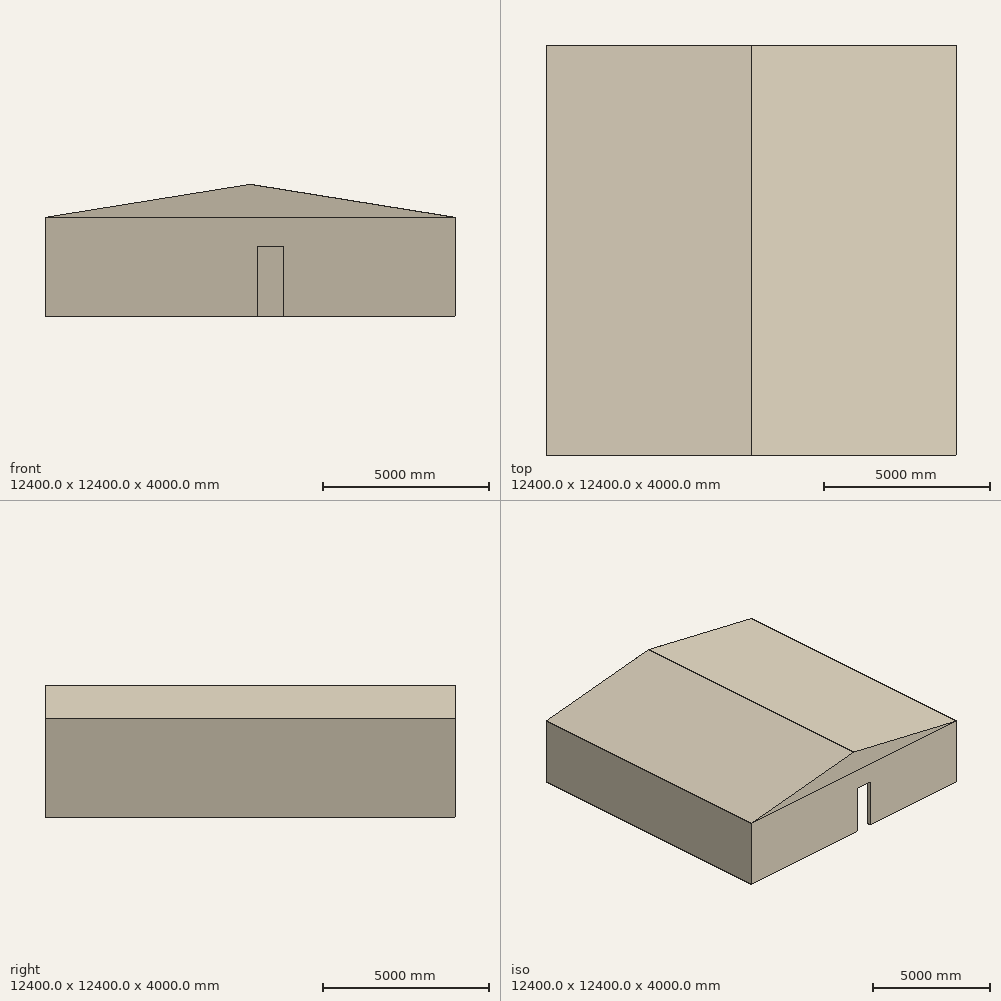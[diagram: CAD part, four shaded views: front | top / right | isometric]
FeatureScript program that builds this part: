
annotation { "Feature Type Name" : "Feature", "Feature Type Description" : "" }
export const myFeature = defineFeature(function(context is Context, id is Id, definition is map)
    precondition{}
    {
        {
            var Q0;
            Q0=qCreatedBy(makeId("Top.planeOp"),FACE);
            var sketch = newSketch(context, id + "F0", { "sketchPlane" : qUnion([Q0])});
            skLineSegment(sketch, "E0.bottom", {"start": v(6000, 6000) * mm, "end": v(5000, 6000) * mm});
            skLineSegment(sketch, "E0.top", {"start": v(6000, -6000) * mm, "end": v(1000, -6000) * mm});
            skLineSegment(sketch, "E0.left", {"start": v(6000, 6000) * mm, "end": v(6000, 2500) * mm});
            skLineSegment(sketch, "E0.right", {"start": v(-6000, 6000) * mm, "end": v(-6000, 2500) * mm});
            skPoint(sketch, "E0.middle", {"position": v(0, 0) * mm});
            skPoint(sketch, "E1", {"position": v(-6000, 0) * mm});
            skPoint(sketch, "E2", {"position": v(6000, 0) * mm});
            skPoint(sketch, "E3", {"position": v(1000, -6000) * mm});
            skPoint(sketch, "E4", {"position": v(-1000, 6000) * mm});
            skPoint(sketch, "E5", {"position": v(1000, 6000) * mm});
            skPoint(sketch, "E6", {"position": v(-1000, -6000) * mm});
            skPoint(sketch, "E7", {"position": v(-1000, 0) * mm});
            skPoint(sketch, "E8", {"position": v(1000, 0) * mm});
            skLineSegment(sketch, "E9", {"start": v(-3900, 1000) * mm, "end": v(-6000, 1000) * mm});
            skLineSegment(sketch, "E10", {"start": v(-3000, 1000) * mm, "end": v(-3000, 6000) * mm});
            skLineSegment(sketch, "E11", {"start": v(-5000, 6000) * mm, "end": v(-5000, 3100) * mm});
            skLineSegment(sketch, "E12", {"start": v(-4900, 2500) * mm, "end": v(-6000, 2500) * mm});
            skLineSegment(sketch, "E13.0", {"start": v(-4900, 6000) * mm, "end": v(-4900, 3100) * mm});
            skLineSegment(sketch, "E14.0", {"start": v(-4900, 2400) * mm, "end": v(-6000, 2400) * mm});
            skLineSegment(sketch, "E15.0", {"start": v(-3900, 1100) * mm, "end": v(-6000, 1100) * mm});
            skLineSegment(sketch, "E16.0", {"start": v(-3100, 1000) * mm, "end": v(-3100, 6000) * mm});
            skLineSegment(sketch, "E17", {"start": v(-4900, 2400) * mm, "end": v(-4900, 2500) * mm});
            skLineSegment(sketch, "E18", {"start": v(-4900, 3100) * mm, "end": v(-5000, 3100) * mm});
            skLineSegment(sketch, "E19", {"start": v(-3900, 1000) * mm, "end": v(-3900, 1100) * mm});
            skLineSegment(sketch, "E20", {"start": v(-3100, 1000) * mm, "end": v(-3000, 1000) * mm});
            skLineSegment(sketch, "E21.0", {"start": v(-6200, 6200) * mm, "end": v(-6200, -6200) * mm});
            skLineSegment(sketch, "E21.1", {"start": v(6200, 6200) * mm, "end": v(-6200, 6200) * mm});
            skLineSegment(sketch, "E21.2", {"start": v(6200, 6200) * mm, "end": v(6200, -6200) * mm});
            skLineSegment(sketch, "E21.3", {"start": v(6200, -6200) * mm, "end": v(1000, -6200) * mm});
            skLineSegment(sketch, "E22.MirrorCS", {"start": v(-1100, 3100) * mm, "end": v(-1000, 3100) * mm});
            skLineSegment(sketch, "E23.MirrorCS", {"start": v(-1100, 2400) * mm, "end": v(-1100, 2500) * mm});
            skLineSegment(sketch, "E24.MirrorCS", {"start": v(-1100, 2400) * mm, "end": v(-50, 2400) * mm});
            skLineSegment(sketch, "E25.MirrorCS", {"start": v(-2100, 1100) * mm, "end": v(-50, 1100) * mm});
            skLineSegment(sketch, "E26.MirrorCS", {"start": v(-2100, 1000) * mm, "end": v(0, 1000) * mm});
            skLineSegment(sketch, "E27.MirrorCS", {"start": v(-1000, 6000) * mm, "end": v(-1000, 3100) * mm});
            skLineSegment(sketch, "E28.MirrorCS", {"start": v(-1100, 2500) * mm, "end": v(-50, 2500) * mm});
            skLineSegment(sketch, "E29.MirrorCS", {"start": v(-1100, 6000) * mm, "end": v(-1100, 3100) * mm});
            skLineSegment(sketch, "E30", {"start": v(0, 6000) * mm, "end": v(0, -6000) * mm, "construction": true});
            skLineSegment(sketch, "E31.MirrorCS", {"start": v(1100, 2400) * mm, "end": v(1100, 2500) * mm});
            skLineSegment(sketch, "E32.MirrorCS", {"start": v(1100, 3100) * mm, "end": v(1000, 3100) * mm});
            skLineSegment(sketch, "E33.MirrorCS", {"start": v(4900, 2400) * mm, "end": v(4900, 2500) * mm});
            skLineSegment(sketch, "E34.MirrorCS", {"start": v(3100, 1000) * mm, "end": v(3000, 1000) * mm});
            skLineSegment(sketch, "E35.MirrorCS", {"start": v(3900, 1000) * mm, "end": v(3900, 1100) * mm});
            skLineSegment(sketch, "E36.MirrorCS", {"start": v(4900, 3100) * mm, "end": v(5000, 3100) * mm});
            skLineSegment(sketch, "E37.MirrorCS", {"start": v(4900, 2400) * mm, "end": v(6000, 2400) * mm});
            skLineSegment(sketch, "E38.MirrorCS", {"start": v(2100, 1000) * mm, "end": v(0, 1000) * mm});
            skLineSegment(sketch, "E39.MirrorCS", {"start": v(2100, 1100) * mm, "end": v(50, 1100) * mm});
            skLineSegment(sketch, "E40.MirrorCS", {"start": v(1100, 6000) * mm, "end": v(1100, 3100) * mm});
            skLineSegment(sketch, "E41.MirrorCS", {"start": v(1100, 2400) * mm, "end": v(50, 2400) * mm});
            skLineSegment(sketch, "E42.MirrorCS", {"start": v(1100, 2500) * mm, "end": v(50, 2500) * mm});
            skLineSegment(sketch, "E43.MirrorCS", {"start": v(3100, 1000) * mm, "end": v(3100, 6000) * mm});
            skLineSegment(sketch, "E44.MirrorCS", {"start": v(3900, 1100) * mm, "end": v(6000, 1100) * mm});
            skLineSegment(sketch, "E45.MirrorCS", {"start": v(4900, 6000) * mm, "end": v(4900, 3100) * mm});
            skLineSegment(sketch, "E46.MirrorCS", {"start": v(4900, 2500) * mm, "end": v(6000, 2500) * mm});
            skLineSegment(sketch, "E47.MirrorCS", {"start": v(5000, 6000) * mm, "end": v(5000, 3100) * mm});
            skLineSegment(sketch, "E48.MirrorCS", {"start": v(3000, 1000) * mm, "end": v(3000, 6000) * mm});
            skLineSegment(sketch, "E49.MirrorCS", {"start": v(1000, 6000) * mm, "end": v(1000, 3100) * mm});
            skLineSegment(sketch, "E50.MirrorCS", {"start": v(3900, 1000) * mm, "end": v(6000, 1000) * mm});
            skLineSegment(sketch, "E51.left", {"start": v(50, 6000) * mm, "end": v(50, 2500) * mm});
            skLineSegment(sketch, "E51.right", {"start": v(-50, 6000) * mm, "end": v(-50, 2500) * mm});
            skPoint(sketch, "E51.middle", {"position": v(0, 4250) * mm});
            skLineSegment(sketch, "E52", {"start": v(-6000, 0) * mm, "end": v(-1900, 0) * mm});
            skLineSegment(sketch, "E53", {"start": v(-1000, 0) * mm, "end": v(-1000, -3200) * mm});
            skLineSegment(sketch, "E54", {"start": v(-4500, -6000) * mm, "end": v(-4500, -5400) * mm});
            skLineSegment(sketch, "E55", {"start": v(-4500, -5400) * mm, "end": v(-1000, -5400) * mm});
            skLineSegment(sketch, "E56", {"start": v(-1000, -5400) * mm, "end": v(-1000, -4000) * mm});
            skLineSegment(sketch, "E57", {"start": v(-6000, -2100) * mm, "end": v(-3100, -2100) * mm});
            skLineSegment(sketch, "E58", {"start": v(6000, 0) * mm, "end": v(1000, 0) * mm});
            skLineSegment(sketch, "E59", {"start": v(6000, -2200) * mm, "end": v(1000, -2200) * mm});
            skLineSegment(sketch, "E60", {"start": v(1000, 0) * mm, "end": v(1000, -1300) * mm});
            skLineSegment(sketch, "E61.0", {"start": v(-6000, -100) * mm, "end": v(-1900, -100) * mm});
            skLineSegment(sketch, "E62.0", {"start": v(-2500, -3100) * mm, "end": v(-2500, -2000) * mm});
            skLineSegment(sketch, "E63.0", {"start": v(-6000, -2000) * mm, "end": v(-3100, -2000) * mm});
            skLineSegment(sketch, "E64.0", {"start": v(-1100, 0) * mm, "end": v(-1100, -3100) * mm});
            skLineSegment(sketch, "E65.0", {"start": v(-1100, -5300) * mm, "end": v(-1100, -4000) * mm});
            skLineSegment(sketch, "E65.1", {"start": v(-4600, -5300) * mm, "end": v(-1100, -5300) * mm});
            skLineSegment(sketch, "E65.2", {"start": v(-4600, -6000) * mm, "end": v(-4600, -5300) * mm});
            skLineSegment(sketch, "E66.0", {"start": v(1100, -100) * mm, "end": v(1100, -1300) * mm});
            skLineSegment(sketch, "E66.1", {"start": v(6000, -100) * mm, "end": v(1100, -100) * mm});
            skLineSegment(sketch, "E67.0", {"start": v(6000, -2100) * mm, "end": v(1000, -2100) * mm});
            skLineSegment(sketch, "E68.0", {"start": v(-2400, -3100) * mm, "end": v(-2400, -2000) * mm});
            skLineSegment(sketch, "E69", {"start": v(-3100, -2000) * mm, "end": v(-3100, -2100) * mm});
            skLineSegment(sketch, "E70", {"start": v(-2500, -2000) * mm, "end": v(-2400, -2000) * mm});
            skLineSegment(sketch, "E71", {"start": v(-1100, 0) * mm, "end": v(-1000, 0) * mm});
            skLineSegment(sketch, "E72", {"start": v(-1100, -4000) * mm, "end": v(-1000, -4000) * mm});
            skLineSegment(sketch, "E73", {"start": v(-1900, -100) * mm, "end": v(-1900, 0) * mm});
            skLineSegment(sketch, "E74", {"start": v(1000, -1300) * mm, "end": v(1100, -1300) * mm});
            skLineSegment(sketch, "E75", {"start": v(1000, -2100) * mm, "end": v(1000, -2200) * mm});
            skLineSegment(sketch, "E76", {"start": v(1000, -6000) * mm, "end": v(1000, -6200) * mm});
            skLineSegment(sketch, "E77", {"start": v(200, -6000) * mm, "end": v(200, -6200) * mm});
            skLineSegment(sketch, "E78", {"start": v(-1100, -3100) * mm, "end": v(-2400, -3100) * mm});
            skLineSegment(sketch, "E79.0", {"start": v(-1000, -3200) * mm, "end": v(-6000, -3200) * mm});
            skLineSegment(sketch, "E80.trimOffspring", {"start": v(-6000, -3200) * mm, "end": v(-6000, -6000) * mm});
            skLineSegment(sketch, "E81.trimOffspring", {"start": v(-2500, -3100) * mm, "end": v(-6000, -3100) * mm});
            skLineSegment(sketch, "E82.trimOffspring", {"start": v(-4600, -6000) * mm, "end": v(-6000, -6000) * mm});
            skLineSegment(sketch, "E83.trimOffspring", {"start": v(-6000, -2100) * mm, "end": v(-6000, -3100) * mm});
            skLineSegment(sketch, "E84.trimOffspring", {"start": v(-6000, 1000) * mm, "end": v(-6000, 0) * mm});
            skLineSegment(sketch, "E85.trimOffspring", {"start": v(-6000, -100) * mm, "end": v(-6000, -2000) * mm});
            skLineSegment(sketch, "E86.trimOffspring", {"start": v(-6000, 2400) * mm, "end": v(-6000, 1100) * mm});
            skLineSegment(sketch, "E87.trimOffspring", {"start": v(-5000, 6000) * mm, "end": v(-6000, 6000) * mm});
            skLineSegment(sketch, "E88.trimOffspring", {"start": v(-1100, 6000) * mm, "end": v(-3000, 6000) * mm});
            skLineSegment(sketch, "E89.trimOffspring", {"start": v(-3100, 6000) * mm, "end": v(-4900, 6000) * mm});
            skLineSegment(sketch, "E90.trimOffspring", {"start": v(-50, 6000) * mm, "end": v(-1000, 6000) * mm});
            skLineSegment(sketch, "E91.trimOffspring", {"start": v(1000, 6000) * mm, "end": v(50, 6000) * mm});
            skLineSegment(sketch, "E92.trimOffspring", {"start": v(3000, 6000) * mm, "end": v(1100, 6000) * mm});
            skLineSegment(sketch, "E93.trimOffspring", {"start": v(4900, 6000) * mm, "end": v(3100, 6000) * mm});
            skLineSegment(sketch, "E94.trimOffspring", {"start": v(6000, -100) * mm, "end": v(6000, -2100) * mm});
            skLineSegment(sketch, "E95.trimOffspring", {"start": v(6000, -2200) * mm, "end": v(6000, -6000) * mm});
            skLineSegment(sketch, "E96.trimOffspring", {"start": v(6000, 2400) * mm, "end": v(6000, 1100) * mm});
            skLineSegment(sketch, "E97.trimOffspring", {"start": v(6000, 1000) * mm, "end": v(6000, 0) * mm});
            skLineSegment(sketch, "E98.trimOffspring", {"start": v(200, -6000) * mm, "end": v(-4500, -6000) * mm});
            skLineSegment(sketch, "E99.trimOffspring", {"start": v(200, -6200) * mm, "end": v(-6200, -6200) * mm});
            skPoint(sketch, "E100.orphan", {"position": v(0, 2500) * mm});
            skLineSegment(sketch, "E101", {"start": v(-50, 2400) * mm, "end": v(-50, 1100) * mm});
            skLineSegment(sketch, "E102", {"start": v(50, 2400) * mm, "end": v(50, 1100) * mm});
            skPoint(sketch, "E103.orphan", {"position": v(0, 2400) * mm});
            skPoint(sketch, "E104.orphan", {"position": v(0, 1100) * mm});
            skLineSegment(sketch, "E105", {"start": v(-2100, 1100) * mm, "end": v(-2200, 1100) * mm});
            skLineSegment(sketch, "E106", {"start": v(-2200, 1100) * mm, "end": v(-2200, 1000) * mm});
            skLineSegment(sketch, "E107", {"start": v(-2200, 1000) * mm, "end": v(-2100, 1000) * mm});
            skLineSegment(sketch, "E108.MirrorCS", {"start": v(2200, 1000) * mm, "end": v(2100, 1000) * mm});
            skLineSegment(sketch, "E109.MirrorCS", {"start": v(2100, 1100) * mm, "end": v(2200, 1100) * mm});
            skLineSegment(sketch, "E110.MirrorCS", {"start": v(2200, 1100) * mm, "end": v(2200, 1000) * mm});
            skSolve(sketch);
        }
        {
            var Q0;
            Q0 = qSketchRegion(id + "F0", true);
            extrude(context, id + "F1", {"entities" : qUnion([Q0]), "depth" : 2120 * mm});
        }
        {
            var Q0;
            Q0=makeQuery(id+"F1.opExtrude","CAP_FACE",FACE,{"disambiguationData":[OSD([sQuery(id+"F0.wireOp",EDGE,"E0.bottom"),sQuery(id+"F0.wireOp",EDGE,"E0.top"),sQuery(id+"F0.wireOp",EDGE,"E0.left"),sQuery(id+"F0.wireOp",EDGE,"E0.right"),sQuery(id+"F0.wireOp",EDGE,"E9"),sQuery(id+"F0.wireOp",EDGE,"E10"),sQuery(id+"F0.wireOp",EDGE,"E11"),sQuery(id+"F0.wireOp",EDGE,"E12"),sQuery(id+"F0.wireOp",EDGE,"E13.0"),sQuery(id+"F0.wireOp",EDGE,"E14.0"),sQuery(id+"F0.wireOp",EDGE,"E15.0"),sQuery(id+"F0.wireOp",EDGE,"E16.0"),sQuery(id+"F0.wireOp",EDGE,"E17"),sQuery(id+"F0.wireOp",EDGE,"E18"),sQuery(id+"F0.wireOp",EDGE,"E19"),sQuery(id+"F0.wireOp",EDGE,"E20"),sQuery(id+"F0.wireOp",EDGE,"E21.0"),sQuery(id+"F0.wireOp",EDGE,"E21.1"),sQuery(id+"F0.wireOp",EDGE,"E21.2"),sQuery(id+"F0.wireOp",EDGE,"E21.3"),sQuery(id+"F0.wireOp",EDGE,"E22.MirrorCS"),sQuery(id+"F0.wireOp",EDGE,"E23.MirrorCS"),sQuery(id+"F0.wireOp",EDGE,"E24.MirrorCS"),sQuery(id+"F0.wireOp",EDGE,"E25.MirrorCS"),sQuery(id+"F0.wireOp",EDGE,"E26.MirrorCS"),sQuery(id+"F0.wireOp",EDGE,"E27.MirrorCS"),sQuery(id+"F0.wireOp",EDGE,"E28.MirrorCS"),sQuery(id+"F0.wireOp",EDGE,"E29.MirrorCS"),sQuery(id+"F0.wireOp",EDGE,"E31.MirrorCS"),sQuery(id+"F0.wireOp",EDGE,"E32.MirrorCS"),sQuery(id+"F0.wireOp",EDGE,"E33.MirrorCS"),sQuery(id+"F0.wireOp",EDGE,"E34.MirrorCS"),sQuery(id+"F0.wireOp",EDGE,"E35.MirrorCS"),sQuery(id+"F0.wireOp",EDGE,"E36.MirrorCS"),sQuery(id+"F0.wireOp",EDGE,"E37.MirrorCS"),sQuery(id+"F0.wireOp",EDGE,"E38.MirrorCS"),sQuery(id+"F0.wireOp",EDGE,"E39.MirrorCS"),sQuery(id+"F0.wireOp",EDGE,"E40.MirrorCS"),sQuery(id+"F0.wireOp",EDGE,"E41.MirrorCS"),sQuery(id+"F0.wireOp",EDGE,"E42.MirrorCS"),sQuery(id+"F0.wireOp",EDGE,"E43.MirrorCS"),sQuery(id+"F0.wireOp",EDGE,"E44.MirrorCS"),sQuery(id+"F0.wireOp",EDGE,"E45.MirrorCS"),sQuery(id+"F0.wireOp",EDGE,"E46.MirrorCS"),sQuery(id+"F0.wireOp",EDGE,"E47.MirrorCS"),sQuery(id+"F0.wireOp",EDGE,"E48.MirrorCS"),sQuery(id+"F0.wireOp",EDGE,"E49.MirrorCS"),sQuery(id+"F0.wireOp",EDGE,"E50.MirrorCS"),sQuery(id+"F0.wireOp",EDGE,"E51.left"),sQuery(id+"F0.wireOp",EDGE,"E51.right"),sQuery(id+"F0.wireOp",EDGE,"E52"),sQuery(id+"F0.wireOp",EDGE,"E53"),sQuery(id+"F0.wireOp",EDGE,"E54"),sQuery(id+"F0.wireOp",EDGE,"E55"),sQuery(id+"F0.wireOp",EDGE,"E56"),sQuery(id+"F0.wireOp",EDGE,"E57"),sQuery(id+"F0.wireOp",EDGE,"E58"),sQuery(id+"F0.wireOp",EDGE,"E59"),sQuery(id+"F0.wireOp",EDGE,"E60"),sQuery(id+"F0.wireOp",EDGE,"E61.0"),sQuery(id+"F0.wireOp",EDGE,"E62.0"),sQuery(id+"F0.wireOp",EDGE,"E63.0"),sQuery(id+"F0.wireOp",EDGE,"E64.0"),sQuery(id+"F0.wireOp",EDGE,"E65.0"),sQuery(id+"F0.wireOp",EDGE,"E65.1"),sQuery(id+"F0.wireOp",EDGE,"E65.2"),sQuery(id+"F0.wireOp",EDGE,"E66.0"),sQuery(id+"F0.wireOp",EDGE,"E66.1"),sQuery(id+"F0.wireOp",EDGE,"E67.0"),sQuery(id+"F0.wireOp",EDGE,"E68.0"),sQuery(id+"F0.wireOp",EDGE,"E69"),sQuery(id+"F0.wireOp",EDGE,"E70"),sQuery(id+"F0.wireOp",EDGE,"E71"),sQuery(id+"F0.wireOp",EDGE,"E72"),sQuery(id+"F0.wireOp",EDGE,"E73"),sQuery(id+"F0.wireOp",EDGE,"E74"),sQuery(id+"F0.wireOp",EDGE,"E75"),sQuery(id+"F0.wireOp",EDGE,"E76"),sQuery(id+"F0.wireOp",EDGE,"E77"),sQuery(id+"F0.wireOp",EDGE,"E78"),sQuery(id+"F0.wireOp",EDGE,"E79.0"),sQuery(id+"F0.wireOp",EDGE,"E80.trimOffspring"),sQuery(id+"F0.wireOp",EDGE,"E81.trimOffspring"),sQuery(id+"F0.wireOp",EDGE,"E82.trimOffspring"),sQuery(id+"F0.wireOp",EDGE,"E83.trimOffspring"),sQuery(id+"F0.wireOp",EDGE,"E84.trimOffspring"),sQuery(id+"F0.wireOp",EDGE,"E85.trimOffspring"),sQuery(id+"F0.wireOp",EDGE,"E86.trimOffspring"),sQuery(id+"F0.wireOp",EDGE,"E87.trimOffspring"),sQuery(id+"F0.wireOp",EDGE,"E88.trimOffspring"),sQuery(id+"F0.wireOp",EDGE,"E89.trimOffspring"),sQuery(id+"F0.wireOp",EDGE,"E90.trimOffspring"),sQuery(id+"F0.wireOp",EDGE,"E91.trimOffspring"),sQuery(id+"F0.wireOp",EDGE,"E92.trimOffspring"),sQuery(id+"F0.wireOp",EDGE,"E93.trimOffspring"),sQuery(id+"F0.wireOp",EDGE,"E94.trimOffspring"),sQuery(id+"F0.wireOp",EDGE,"E95.trimOffspring"),sQuery(id+"F0.wireOp",EDGE,"E96.trimOffspring"),sQuery(id+"F0.wireOp",EDGE,"E97.trimOffspring"),sQuery(id+"F0.wireOp",EDGE,"E98.trimOffspring"),sQuery(id+"F0.wireOp",EDGE,"E99.trimOffspring"),sQuery(id+"F0.wireOp",EDGE,"E101"),sQuery(id+"F0.wireOp",EDGE,"E102"),sQuery(id+"F0.wireOp",EDGE,"E105"),sQuery(id+"F0.wireOp",EDGE,"E106"),sQuery(id+"F0.wireOp",EDGE,"E107"),sQuery(id+"F0.wireOp",EDGE,"E108.MirrorCS"),sQuery(id+"F0.wireOp",EDGE,"E109.MirrorCS"),sQuery(id+"F0.wireOp",EDGE,"E110.MirrorCS")])],"isStart":false});
            var sketch = newSketch(context, id + "F2", { "sketchPlane" : qUnion([Q0])});
            skLineSegment(sketch, "E111.0", {"start": v(-6200, 6200) * mm, "end": v(-6200, -6200) * mm});
            skLineSegment(sketch, "E112.0", {"start": v(6200, 6200) * mm, "end": v(-6200, 6200) * mm});
            skLineSegment(sketch, "E113.0", {"start": v(6200, 6200) * mm, "end": v(6200, -6200) * mm});
            skLineSegment(sketch, "E114.0", {"start": v(-5000, 6000) * mm, "end": v(-6000, 6000) * mm});
            skLineSegment(sketch, "E115.0", {"start": v(-6000, 6000) * mm, "end": v(-6000, 2500) * mm});
            skLineSegment(sketch, "E116.0", {"start": v(-4900, 2400) * mm, "end": v(-6000, 2400) * mm});
            skLineSegment(sketch, "E117.0", {"start": v(-6000, 2400) * mm, "end": v(-6000, 1100) * mm});
            skLineSegment(sketch, "E118.0", {"start": v(-6000, 1000) * mm, "end": v(-6000, 0) * mm});
            skLineSegment(sketch, "E119.0", {"start": v(-3100, 6000) * mm, "end": v(-4900, 6000) * mm});
            skLineSegment(sketch, "E120.0", {"start": v(-1100, 6000) * mm, "end": v(-3000, 6000) * mm});
            skLineSegment(sketch, "E121.0", {"start": v(-50, 6000) * mm, "end": v(-1000, 6000) * mm});
            skLineSegment(sketch, "E122.0", {"start": v(1000, 6000) * mm, "end": v(50, 6000) * mm});
            skLineSegment(sketch, "E123.0", {"start": v(3000, 6000) * mm, "end": v(1100, 6000) * mm});
            skLineSegment(sketch, "E124.0", {"start": v(4900, 6000) * mm, "end": v(3100, 6000) * mm});
            skLineSegment(sketch, "E125.0", {"start": v(6000, 6000) * mm, "end": v(5000, 6000) * mm});
            skLineSegment(sketch, "E126.0", {"start": v(6000, 6000) * mm, "end": v(6000, 2500) * mm});
            skLineSegment(sketch, "E127.0", {"start": v(4900, 2400) * mm, "end": v(6000, 2400) * mm});
            skLineSegment(sketch, "E128.0", {"start": v(1100, 2400) * mm, "end": v(50, 2400) * mm});
            skLineSegment(sketch, "E129.0", {"start": v(50, 2400) * mm, "end": v(50, 1100) * mm});
            skLineSegment(sketch, "E130.0", {"start": v(-50, 2400) * mm, "end": v(-50, 1100) * mm});
            skLineSegment(sketch, "E131.0", {"start": v(-1100, 2400) * mm, "end": v(-50, 2400) * mm});
            skLineSegment(sketch, "E132.0", {"start": v(6000, 1000) * mm, "end": v(6000, 0) * mm});
            skLineSegment(sketch, "E133.0", {"start": v(6000, -2200) * mm, "end": v(1000, -2200) * mm});
            skLineSegment(sketch, "E134.0", {"start": v(6000, -100) * mm, "end": v(6000, -2100) * mm});
            skLineSegment(sketch, "E135.0", {"start": v(6000, 0) * mm, "end": v(1000, 0) * mm});
            skLineSegment(sketch, "E136.0", {"start": v(6000, -100) * mm, "end": v(1100, -100) * mm});
            skLineSegment(sketch, "E137.0", {"start": v(-2400, -3100) * mm, "end": v(-2400, -2000) * mm});
            skLineSegment(sketch, "E138.0", {"start": v(-1100, -3100) * mm, "end": v(-2400, -3100) * mm});
            skLineSegment(sketch, "E139.0", {"start": v(-2500, -3100) * mm, "end": v(-6000, -3100) * mm});
            skLineSegment(sketch, "E140.0", {"start": v(-6000, -2100) * mm, "end": v(-6000, -3100) * mm});
            skLineSegment(sketch, "E141.0", {"start": v(-6000, -100) * mm, "end": v(-6000, -2000) * mm});
            skLineSegment(sketch, "E142.0", {"start": v(-6000, -3200) * mm, "end": v(-6000, -6000) * mm});
            skLineSegment(sketch, "E143.0", {"start": v(-4600, -6000) * mm, "end": v(-6000, -6000) * mm});
            skLineSegment(sketch, "E144.0", {"start": v(-4600, -6000) * mm, "end": v(-4600, -5300) * mm});
            skLineSegment(sketch, "E145.0", {"start": v(-4600, -5300) * mm, "end": v(-1100, -5300) * mm});
            skLineSegment(sketch, "E146.0", {"start": v(-4500, -6000) * mm, "end": v(-4500, -5400) * mm});
            skLineSegment(sketch, "E147.0", {"start": v(6000, -2200) * mm, "end": v(6000, -6000) * mm});
            skLineSegment(sketch, "E148", {"start": v(-4900, 2400) * mm, "end": v(-4900, 6000) * mm});
            skLineSegment(sketch, "E149", {"start": v(-5000, 6000) * mm, "end": v(-5000, 2500) * mm});
            skLineSegment(sketch, "E150", {"start": v(-6000, 2500) * mm, "end": v(-5000, 2500) * mm});
            skLineSegment(sketch, "E151", {"start": v(-6000, 1100) * mm, "end": v(-3100, 1100) * mm});
            skLineSegment(sketch, "E152", {"start": v(-3100, 1100) * mm, "end": v(-3100, 6000) * mm});
            skLineSegment(sketch, "E153.0", {"start": v(-50, 6000) * mm, "end": v(-50, 2500) * mm});
            skLineSegment(sketch, "E154.0", {"start": v(50, 6000) * mm, "end": v(50, 2500) * mm});
            skLineSegment(sketch, "E155", {"start": v(-1000, 6000) * mm, "end": v(-1000, 2500) * mm});
            skLineSegment(sketch, "E156", {"start": v(-1000, 2500) * mm, "end": v(-50, 2500) * mm});
            skLineSegment(sketch, "E157", {"start": v(-1100, 2400) * mm, "end": v(-1100, 6000) * mm});
            skLineSegment(sketch, "E158", {"start": v(1000, 6000) * mm, "end": v(1000, 2500) * mm});
            skLineSegment(sketch, "E159", {"start": v(50, 2500) * mm, "end": v(1000, 2500) * mm});
            skLineSegment(sketch, "E160", {"start": v(1100, 2400) * mm, "end": v(1100, 6000) * mm});
            skLineSegment(sketch, "E161", {"start": v(5000, 6000) * mm, "end": v(5000, 2500) * mm});
            skLineSegment(sketch, "E162", {"start": v(6000, 2500) * mm, "end": v(5000, 2500) * mm});
            skLineSegment(sketch, "E163", {"start": v(4900, 2400) * mm, "end": v(4900, 6000) * mm});
            skLineSegment(sketch, "E164.0", {"start": v(6000, 2400) * mm, "end": v(6000, 1100) * mm});
            skLineSegment(sketch, "E165", {"start": v(3100, 6000) * mm, "end": v(3100, 1100) * mm});
            skLineSegment(sketch, "E166", {"start": v(6000, 1100) * mm, "end": v(3100, 1100) * mm});
            skLineSegment(sketch, "E167", {"start": v(-3000, 6000) * mm, "end": v(-3000, 1100) * mm});
            skLineSegment(sketch, "E168", {"start": v(3000, 6000) * mm, "end": v(3000, 1100) * mm});
            skLineSegment(sketch, "E169", {"start": v(50, 1100) * mm, "end": v(3000, 1100) * mm});
            skLineSegment(sketch, "E170", {"start": v(-50, 1100) * mm, "end": v(-3000, 1100) * mm});
            skLineSegment(sketch, "E171", {"start": v(-6000, 1000) * mm, "end": v(6000, 1000) * mm});
            skLineSegment(sketch, "E172", {"start": v(-6000, -2100) * mm, "end": v(-2500, -2100) * mm});
            skLineSegment(sketch, "E173", {"start": v(-2500, -2100) * mm, "end": v(-2500, -3100) * mm});
            skLineSegment(sketch, "E174", {"start": v(-2400, -2000) * mm, "end": v(-6000, -2000) * mm});
            skLineSegment(sketch, "E175", {"start": v(-6000, -100) * mm, "end": v(-1100, -100) * mm});
            skLineSegment(sketch, "E176", {"start": v(-1100, -3100) * mm, "end": v(-1100, -100) * mm});
            skLineSegment(sketch, "E177", {"start": v(-1000, 0) * mm, "end": v(-6000, 0) * mm});
            skLineSegment(sketch, "E178", {"start": v(1100, -100) * mm, "end": v(1100, -2100) * mm});
            skLineSegment(sketch, "E179", {"start": v(1100, -2100) * mm, "end": v(6000, -2100) * mm});
            skLineSegment(sketch, "E180", {"start": v(1000, -2200) * mm, "end": v(1000, 0) * mm});
            skLineSegment(sketch, "E181", {"start": v(-1100, -3200) * mm, "end": v(-6000, -3200) * mm});
            skLineSegment(sketch, "E182", {"start": v(-1100, -3200) * mm, "end": v(-1100, -5300) * mm});
            skLineSegment(sketch, "E183", {"start": v(-4500, -5400) * mm, "end": v(-1100, -5400) * mm});
            skLineSegment(sketch, "E184", {"start": v(-1100, -6000) * mm, "end": v(-1100, -5400) * mm});
            skLineSegment(sketch, "E185", {"start": v(-1100, -6000) * mm, "end": v(-4500, -6000) * mm});
            skLineSegment(sketch, "E186", {"start": v(-1000, 0) * mm, "end": v(-1000, -6000) * mm});
            skLineSegment(sketch, "E187", {"start": v(-1000, -6000) * mm, "end": v(6000, -6000) * mm});
            skLineSegment(sketch, "E188", {"start": v(-6200, -6200) * mm, "end": v(6200, -6200) * mm});
            skSolve(sketch);
        }
        {
            var Q0;
            {var subQ10=sQuery(id+"F2.wireOp",EDGE,"E111.0");Q0=makeQuery(id+"F2.imprint","IMPRINT",FACE,{"disambiguationData":[TD([[makeQuery(id+"F2.imprint","IMPRINT",EDGE,{"derivedFrom":subQ10}),1.0]])]});}
            var Q1;
            {var subQ1=makeQuery(id+"F1.opExtrude","CAP_EDGE",EDGE,{"disambiguationData":[OSD([sQuery(id+"F0.wireOp",EDGE,"E76")])],"isStart":false});Q1=makeQuery(id+"F2.imprint","IMPRINT",FACE,{"disambiguationData":[TD([[makeQuery(id+"F2.imprint","IMPRINT",EDGE,{"derivedFrom":subQ1}),-1.0]])]});}
            var Q2;
            {var subQ1=makeQuery(id+"F1.opExtrude","CAP_EDGE",EDGE,{"disambiguationData":[OSD([sQuery(id+"F0.wireOp",EDGE,"E72")])],"isStart":false});Q2=makeQuery(id+"F2.imprint","IMPRINT",FACE,{"disambiguationData":[TD([[makeQuery(id+"F2.imprint","IMPRINT",EDGE,{"derivedFrom":subQ1}),1.0]])]});}
            var Q3;
            {var subQ0=sQuery(id+"F2.wireOp",EDGE,"E184");Q3=makeQuery(id+"F2.imprint","IMPRINT",FACE,{"disambiguationData":[TD([[makeQuery(id+"F2.imprint","IMPRINT",EDGE,{"derivedFrom":subQ0}),-1.0]])]});}
            var Q4;
            {var subQ1=makeQuery(id+"F1.opExtrude","CAP_EDGE",EDGE,{"disambiguationData":[OSD([sQuery(id+"F0.wireOp",EDGE,"E69")])],"isStart":false});Q4=makeQuery(id+"F2.imprint","IMPRINT",FACE,{"disambiguationData":[TD([[makeQuery(id+"F2.imprint","IMPRINT",EDGE,{"derivedFrom":subQ1}),1.0]])]});}
            var Q5;
            {var subQ1=makeQuery(id+"F1.opExtrude","CAP_EDGE",EDGE,{"disambiguationData":[OSD([sQuery(id+"F0.wireOp",EDGE,"E73")])],"isStart":false});Q5=makeQuery(id+"F2.imprint","IMPRINT",FACE,{"disambiguationData":[TD([[makeQuery(id+"F2.imprint","IMPRINT",EDGE,{"derivedFrom":subQ1}),-1.0]])]});}
            var Q6;
            {var subQ1=makeQuery(id+"F1.opExtrude","CAP_EDGE",EDGE,{"disambiguationData":[OSD([sQuery(id+"F0.wireOp",EDGE,"E74")])],"isStart":false});Q6=makeQuery(id+"F2.imprint","IMPRINT",FACE,{"disambiguationData":[TD([[makeQuery(id+"F2.imprint","IMPRINT",EDGE,{"derivedFrom":subQ1}),-1.0]])]});}
            var Q7;
            {var subQ1=makeQuery(id+"F1.opExtrude","CAP_EDGE",EDGE,{"disambiguationData":[OSD([sQuery(id+"F0.wireOp",EDGE,"E106")])],"isStart":false});Q7=makeQuery(id+"F2.imprint","IMPRINT",FACE,{"disambiguationData":[TD([[makeQuery(id+"F2.imprint","IMPRINT",EDGE,{"derivedFrom":subQ1}),-1.0]])]});}
            var Q8;
            {var subQ1=makeQuery(id+"F1.opExtrude","CAP_EDGE",EDGE,{"disambiguationData":[OSD([sQuery(id+"F0.wireOp",EDGE,"E19")])],"isStart":false});Q8=makeQuery(id+"F2.imprint","IMPRINT",FACE,{"disambiguationData":[TD([[makeQuery(id+"F2.imprint","IMPRINT",EDGE,{"derivedFrom":subQ1}),-1.0]])]});}
            var Q9;
            {var subQ3=makeQuery(id+"F1.opExtrude","CAP_EDGE",EDGE,{"disambiguationData":[OSD([sQuery(id+"F0.wireOp",EDGE,"E18")])],"isStart":false});Q9=makeQuery(id+"F2.imprint","IMPRINT",FACE,{"disambiguationData":[TD([[makeQuery(id+"F2.imprint","IMPRINT",EDGE,{"derivedFrom":subQ3}),1.0]])]});}
            var Q10;
            {var subQ1=makeQuery(id+"F1.opExtrude","CAP_EDGE",EDGE,{"disambiguationData":[OSD([sQuery(id+"F0.wireOp",EDGE,"E22.MirrorCS")])],"isStart":false});Q10=makeQuery(id+"F2.imprint","IMPRINT",FACE,{"disambiguationData":[TD([[makeQuery(id+"F2.imprint","IMPRINT",EDGE,{"derivedFrom":subQ1}),-1.0]])]});}
            var Q11;
            {var subQ1=makeQuery(id+"F1.opExtrude","CAP_EDGE",EDGE,{"disambiguationData":[OSD([sQuery(id+"F0.wireOp",EDGE,"E32.MirrorCS")])],"isStart":false});Q11=makeQuery(id+"F2.imprint","IMPRINT",FACE,{"disambiguationData":[TD([[makeQuery(id+"F2.imprint","IMPRINT",EDGE,{"derivedFrom":subQ1}),1.0]])]});}
            var Q12;
            {var subQ1=makeQuery(id+"F1.opExtrude","CAP_EDGE",EDGE,{"disambiguationData":[OSD([sQuery(id+"F0.wireOp",EDGE,"E35.MirrorCS")])],"isStart":false});Q12=makeQuery(id+"F2.imprint","IMPRINT",FACE,{"disambiguationData":[TD([[makeQuery(id+"F2.imprint","IMPRINT",EDGE,{"derivedFrom":subQ1}),1.0]])]});}
            var Q13;
            {var subQ1=makeQuery(id+"F1.opExtrude","CAP_EDGE",EDGE,{"disambiguationData":[OSD([sQuery(id+"F0.wireOp",EDGE,"E36.MirrorCS")])],"isStart":false});Q13=makeQuery(id+"F2.imprint","IMPRINT",FACE,{"disambiguationData":[TD([[makeQuery(id+"F2.imprint","IMPRINT",EDGE,{"derivedFrom":subQ1}),-1.0]])]});}
            var Q14;
            {var subQ1=makeQuery(id+"F1.opExtrude","CAP_EDGE",EDGE,{"disambiguationData":[OSD([sQuery(id+"F0.wireOp",EDGE,"E110.MirrorCS")])],"isStart":false});Q14=makeQuery(id+"F2.imprint","IMPRINT",FACE,{"disambiguationData":[TD([[makeQuery(id+"F2.imprint","IMPRINT",EDGE,{"derivedFrom":subQ1}),1.0]])]});}
            extrude(context, id + "F3", {"entities" : qUnion([Q0, Q1, Q2, Q3, Q4, Q5, Q6, Q7, Q8, Q9, Q10, Q11, Q12, Q13, Q14]), "operationType" : NewBodyOperationType.ADD, "depth" : 3000 * mm - 2120 * mm});
        }
        {
            var Q0;
            Q0=qCreatedBy(makeId("Front.planeOp"),FACE);
            var sketch = newSketch(context, id + "F4", { "sketchPlane" : qUnion([Q0])});
            skPoint(sketch, "E189.0", {"position": v(-6200, 3000) * mm});
            skPoint(sketch, "E189.1", {"position": v(6200, 3000) * mm});
            skLineSegment(sketch, "E190", {"start": v(-6200, 3000) * mm, "end": v(0, 4000) * mm});
            skLineSegment(sketch, "E191", {"start": v(0, 4000) * mm, "end": v(6200, 3000) * mm});
            skLineSegment(sketch, "E192", {"start": v(-6200, 3000) * mm, "end": v(6200, 3000) * mm});
            skSolve(sketch);
        }
        {
            var Q0;
            Q0 = qSketchRegion(id + "F4", true);
            var Q1;
            Q1=makeQuery(id+"F1.opExtrude","SWEPT_FACE",FACE,{"disambiguationData":[OSD([sQuery(id+"F0.wireOp",EDGE,"E99.trimOffspring")])]});
            var Q2;
            Q2=makeQuery(id+"F1.opExtrude","SWEPT_FACE",FACE,{"disambiguationData":[OSD([sQuery(id+"F0.wireOp",EDGE,"E21.1")])]});
            extrude(context, id + "F5", {"entities" : qUnion([Q0]), "endBound" : BoundingType.UP_TO_SURFACE, "endBoundEntityFace" : qUnion([Q1]), "depth" : 25 * mm, "hasSecondDirection" : true, "secondDirectionBound" : SecondDirectionBoundingType.UP_TO_SURFACE, "secondDirectionOppositeDirection" : true, "secondDirectionBoundEntityFace" : qUnion([Q2]), "secondDirectionDepth" : 25 * mm});
        }
    });
